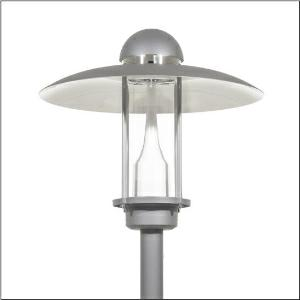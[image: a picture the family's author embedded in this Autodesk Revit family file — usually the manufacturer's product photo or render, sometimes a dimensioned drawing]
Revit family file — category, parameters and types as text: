
# Revit family: city-light_elegance_iq___pl1_2s_5xa5265jf14h_a7e3
name_source: partatom
category: Lighting Fixtures
units: mm (PartAtom-declared; Revit-internal decimal feet)

## family parameters
Cut with Voids When Loaded = No
Host = Face
Light Source = No
Part Type = Normal
Room Calculation Point = No
Round Connector Dimension = Use Diameter
Shared = No

## types (1)
- --- (1 x LED, 2840 lm, 19.3 W, 3000K)
    Apparent Load = 19 VA
    CIE Flux Codes = 24 63 94 98 100
    Color Rendering = 70
    Color Temperature = 3000K
    Default Elevation = 1800 mm
    Description = City-Light Elegance iQ, mast luminaire, Module 540 iQ-SR, primary light control with 3 zone facetted reflector, of plastic, silver coated, highly specular, structured, primary optical cover: cover, of PMMA, transparent, light distribution: PL1.2s, light emission: direct distribution, primary light characteristic: symmetric, installation type: post-top, LED, High Power LED, rated luminous flux: 2.840lm, luminous efficacy: 147lm/W, light colour: 730, colour temperature: 3000K, control gear: ECG iQ, control: Auto-Match, Temp-Guard, Lumen-Switch, Night-Set, Smart-Wire, Light-Fading, Desk-Remote (wireless, voltage-free reading and setting of iQ features in the workshop via application-optimized NFC function/RFID function), optimised constant luminous flux control (CLO 2.0), Street-Remote, pre-setting: logarithmic dimming characteristic, with terminal, 6-pole, max. 2.5mm², mains connection: 230..240V, AC, 50/60Hz, start of lifetime: 19W, end of service life: 21W, reduction: 10W, luminaire housing, upper part, of aluminium, coated, Siteco® metallic grey (DB 702S), diameter: 750mm, height: 675mm, spigot size: d x l = 76 x 70mm (post-top) | with reducer (optional accessory) 60 x 70mm, post-top mast mounting element, of diecast aluminium, coated, Siteco® metallic grey (DB 702S), Module 540 iQ-SR, traffic white (RAL 9016), equipment: standard, protection rating (complete): IP65, insulation class (complete): insulation class II (safety insulation), certification: CE, ENEC, VDE, packaging unit: 1 piece

Light Distribution: PL1.2s
    Height = 675 mm
    Lamp = 1 x LED
    Lamp Light Flux = 2840 lm
    Lamp Power = 19.3 W
    Lamp count = 1
    Length = 750 mm
    Luminous efficacy = 147 lm/W
    Manufacturer = Siteco
    ModVariant = No
    Model = 5XA5265JF14H
    Number of Poles = 1
    OnlyDefault = Yes
    Power Factor = 1
    Product Name = City-Light Elegance iQ | PL1.2s
    Product group = mast luminaire | pylon top
    ProductGroupID = 6100
    Protection Class = Protection class II
    Protection Degree = IP 65
    RLX_Detail_Level = 1
    RLX_Emergency_Light_Flux = 0 lm
    RLX_Emergency_Type = 0
    RLX_Emergency_Type_DB = No
    RlxData = <blob elided: 72713 chars, md5=4c554169>
    Socket = socket
    Standby Power = 0 W
    System Light Flux = 2840 lm
    System Power = 19 W
    Type Comments = factory setting: luminous flux: 100 % | dim-lin: 254 | 403 mA
    Type Image = l_1006912.jpg
    URL = http://relux.com
    VarID = @adj_115305
    Voltage = 0 V
    Weight = 0.00 kg
    Width = 0 mm  [stored 0 ft]

note: [stored X ft] marks values corroborated as IEEE doubles in the binary element streams (Revit-internal decimal feet)

## geometry (parser evidence)
native form markers: Blend x4, Sweep x10
no freeform markers — native parametric forms only
